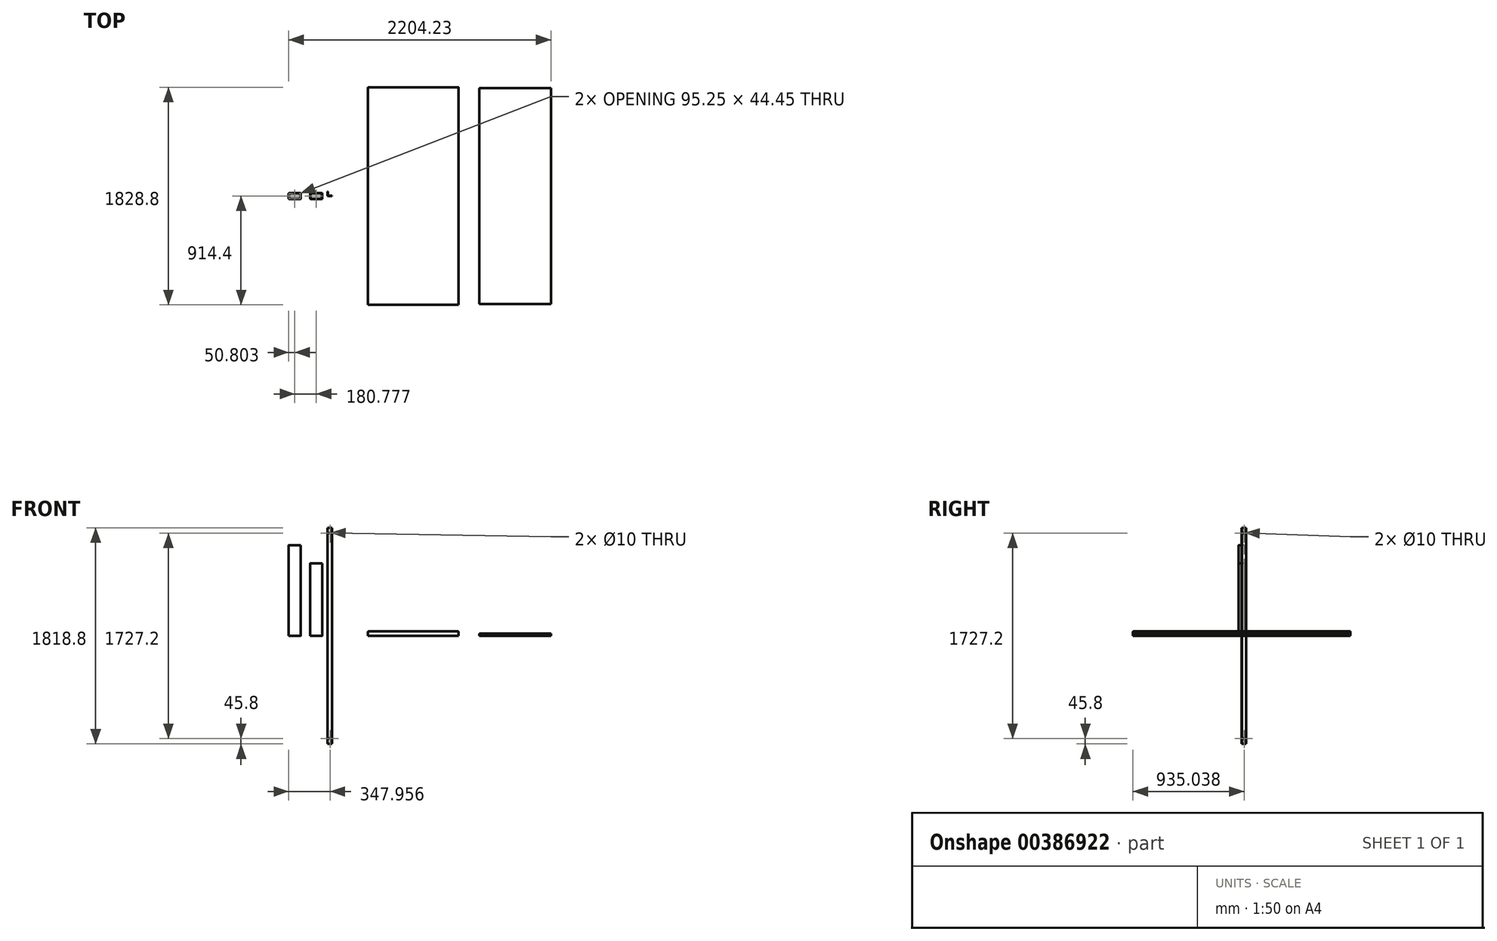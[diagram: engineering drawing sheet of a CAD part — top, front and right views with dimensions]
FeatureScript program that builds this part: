
annotation { "Feature Type Name" : "Feature", "Feature Type Description" : "" }
export const myFeature = defineFeature(function(context is Context, id is Id, definition is map)
    precondition{}
    {
        {
            var Q0;
            Q0=qCreatedBy(makeId("Top.planeOp"),FACE);
            var sketch = newSketch(context, id + "F0", { "sketchPlane" : qUnion([Q0])});
            skPoint(sketch, "E0.middle", {"position": v(-180.78, 0) * mm});
            skLineSegment(sketch, "E1.bottom", {"start": v(-134.98, 25.4) * mm, "end": v(-226.58, 25.4) * mm});
            skLineSegment(sketch, "E1.top", {"start": v(-134.98, -25.4) * mm, "end": v(-226.58, -25.4) * mm});
            skLineSegment(sketch, "E1.left", {"start": v(-129.98, 20.4) * mm, "end": v(-129.98, -20.4) * mm});
            skLineSegment(sketch, "E1.right", {"start": v(-231.58, 20.4) * mm, "end": v(-231.58, -20.4) * mm});
            skLineSegment(sketch, "E2.0", {"start": v(-138.15, 22.22) * mm, "end": v(-223.4, 22.22) * mm});
            skLineSegment(sketch, "E2.1", {"start": v(-133.15, 17.22) * mm, "end": v(-133.15, -17.22) * mm});
            skLineSegment(sketch, "E2.2", {"start": v(-138.15, -22.23) * mm, "end": v(-223.4, -22.23) * mm});
            skLineSegment(sketch, "E2.3", {"start": v(-228.4, 17.22) * mm, "end": v(-228.4, -17.22) * mm});
            skPoint(sketch, "E3.visualSharp", {"position": v(-231.58, 25.4) * mm});
            skArc(sketch, "E3.filletArc", {"start": v(-226.58, 25.4) * mm, "mid": v(-230.11, 23.94) * mm, "end": v(-231.58, 20.4) * mm});
            skPoint(sketch, "E4.visualSharp", {"position": v(-129.98, 25.4) * mm});
            skArc(sketch, "E4.filletArc", {"start": v(-129.98, 20.4) * mm, "mid": v(-131.44, 23.94) * mm, "end": v(-134.98, 25.4) * mm});
            skPoint(sketch, "E5.visualSharp", {"position": v(-129.98, -25.4) * mm});
            skArc(sketch, "E5.filletArc", {"start": v(-134.98, -25.4) * mm, "mid": v(-131.44, -23.94) * mm, "end": v(-129.98, -20.4) * mm});
            skPoint(sketch, "E6.visualSharp", {"position": v(-231.58, -25.4) * mm});
            skArc(sketch, "E6.filletArc", {"start": v(-231.58, -20.4) * mm, "mid": v(-230.11, -23.94) * mm, "end": v(-226.58, -25.4) * mm});
            skPoint(sketch, "E7.visualSharp", {"position": v(-228.4, -22.23) * mm});
            skArc(sketch, "E7.filletArc", {"start": v(-228.4, -17.22) * mm, "mid": v(-226.94, -20.76) * mm, "end": v(-223.4, -22.23) * mm});
            skPoint(sketch, "E8.visualSharp", {"position": v(-228.4, 22.22) * mm});
            skArc(sketch, "E8.filletArc", {"start": v(-223.4, 22.22) * mm, "mid": v(-226.94, 20.76) * mm, "end": v(-228.4, 17.22) * mm});
            skPoint(sketch, "E9.visualSharp", {"position": v(-133.15, 22.22) * mm});
            skArc(sketch, "E9.filletArc", {"start": v(-133.15, 17.22) * mm, "mid": v(-134.62, 20.76) * mm, "end": v(-138.15, 22.22) * mm});
            skPoint(sketch, "E10.visualSharp", {"position": v(-133.15, -22.23) * mm});
            skArc(sketch, "E10.filletArc", {"start": v(-138.15, -22.23) * mm, "mid": v(-134.62, -20.76) * mm, "end": v(-133.15, -17.22) * mm});
            skSolve(sketch);
        }
        {
            var Q0;
            Q0=makeQuery(id+"F0.imprint","IMPRINT",FACE,{"disambiguationData":[TD([[makeQuery(id+"F0.imprint","IMPRINT",EDGE,{"derivedFrom":sQuery(id+"F0.wireOp",EDGE,"E1.bottom")}),1.0]])]});
            extrude(context, id + "F1", {"entities" : qUnion([Q0]), "depth" : 762 * mm});
        }
        {
            var Q0;
            Q0=qCreatedBy(makeId("Top.planeOp"),FACE);
            var sketch = newSketch(context, id + "F2", { "sketchPlane" : qUnion([Q0])});
            skLineSegment(sketch, "E11.bottom", {"start": v(45.8, 25.4) * mm, "end": v(-45.8, 25.4) * mm});
            skLineSegment(sketch, "E11.top", {"start": v(45.8, -25.4) * mm, "end": v(-45.8, -25.4) * mm});
            skLineSegment(sketch, "E11.left", {"start": v(50.8, 20.4) * mm, "end": v(50.8, -20.4) * mm});
            skLineSegment(sketch, "E11.right", {"start": v(-50.8, 20.4) * mm, "end": v(-50.8, -20.4) * mm});
            skPoint(sketch, "E11.middle", {"position": v(0, 0) * mm});
            skLineSegment(sketch, "E12.0", {"start": v(42.62, 22.23) * mm, "end": v(-42.62, 22.23) * mm});
            skLineSegment(sketch, "E12.1", {"start": v(47.62, 17.23) * mm, "end": v(47.62, -17.23) * mm});
            skLineSegment(sketch, "E12.2", {"start": v(42.62, -22.23) * mm, "end": v(-42.62, -22.23) * mm});
            skLineSegment(sketch, "E12.3", {"start": v(-47.62, 17.23) * mm, "end": v(-47.62, -17.23) * mm});
            skPoint(sketch, "E13.visualSharp", {"position": v(-50.8, 25.4) * mm});
            skArc(sketch, "E13.filletArc", {"start": v(-45.8, 25.4) * mm, "mid": v(-49.34, 23.94) * mm, "end": v(-50.8, 20.4) * mm});
            skPoint(sketch, "E14.visualSharp", {"position": v(-47.62, 22.23) * mm});
            skArc(sketch, "E14.filletArc", {"start": v(-42.62, 22.23) * mm, "mid": v(-46.16, 20.76) * mm, "end": v(-47.62, 17.23) * mm});
            skPoint(sketch, "E15.visualSharp", {"position": v(-47.62, -22.23) * mm});
            skArc(sketch, "E15.filletArc", {"start": v(-47.62, -17.23) * mm, "mid": v(-46.16, -20.76) * mm, "end": v(-42.62, -22.22) * mm});
            skPoint(sketch, "E16.visualSharp", {"position": v(-50.8, -25.4) * mm});
            skArc(sketch, "E16.filletArc", {"start": v(-50.8, -20.4) * mm, "mid": v(-49.34, -23.94) * mm, "end": v(-45.8, -25.4) * mm});
            skPoint(sketch, "E17.visualSharp", {"position": v(47.62, -22.23) * mm});
            skArc(sketch, "E17.filletArc", {"start": v(42.62, -22.23) * mm, "mid": v(46.16, -20.76) * mm, "end": v(47.62, -17.23) * mm});
            skPoint(sketch, "E18.visualSharp", {"position": v(47.62, 22.23) * mm});
            skArc(sketch, "E18.filletArc", {"start": v(47.62, 17.23) * mm, "mid": v(46.16, 20.76) * mm, "end": v(42.62, 22.22) * mm});
            skPoint(sketch, "E19.visualSharp", {"position": v(50.8, 25.4) * mm});
            skArc(sketch, "E19.filletArc", {"start": v(50.8, 20.4) * mm, "mid": v(49.34, 23.94) * mm, "end": v(45.8, 25.4) * mm});
            skPoint(sketch, "E20.visualSharp", {"position": v(50.8, -25.4) * mm});
            skArc(sketch, "E20.filletArc", {"start": v(45.8, -25.4) * mm, "mid": v(49.34, -23.94) * mm, "end": v(50.8, -20.4) * mm});
            skSolve(sketch);
        }
        {
            var Q0;
            Q0 = qSketchRegion(id + "F2", true);
            extrude(context, id + "F3", {"entities" : qUnion([Q0]), "depth" : 609.6 * mm});
        }
        {
            var Q0;
            Q0=qCreatedBy(makeId("Top.planeOp"),FACE);
            var sketch = newSketch(context, id + "F4", { "sketchPlane" : qUnion([Q0])});
            skLineSegment(sketch, "E21", {"start": v(95.74, 0) * mm, "end": v(95.74, 38.1) * mm});
            skLineSegment(sketch, "E22", {"start": v(95.74, 38.1) * mm, "end": v(98.91, 38.1) * mm});
            skLineSegment(sketch, "E23", {"start": v(98.91, 38.1) * mm, "end": v(98.91, 3.18) * mm});
            skLineSegment(sketch, "E24", {"start": v(98.91, 3.18) * mm, "end": v(133.84, 3.18) * mm});
            skLineSegment(sketch, "E25", {"start": v(133.84, 3.18) * mm, "end": v(133.84, 0) * mm});
            skLineSegment(sketch, "E26", {"start": v(133.84, 0) * mm, "end": v(95.74, 0) * mm});
            skSolve(sketch);
        }
        {
            var Q0;
            Q0 = qSketchRegion(id + "F4", true);
            extrude(context, id + "F5", {"entities" : qUnion([Q0]), "depth" : 1828.8 * mm - 10 * mm, "symmetric" : true});
        }
        {
            var Q0;
            Q0=qCreatedBy(makeId("Front.planeOp"),FACE);
            var sketch = newSketch(context, id + "F6", { "sketchPlane" : qUnion([Q0])});
            skLineSegment(sketch, "E27.bottom", {"start": v(433.88, 0) * mm, "end": v(1195.88, 0) * mm});
            skLineSegment(sketch, "E27.top", {"start": v(433.88, 38.1) * mm, "end": v(1195.88, 38.1) * mm});
            skLineSegment(sketch, "E27.left", {"start": v(433.88, 0) * mm, "end": v(433.88, 38.1) * mm});
            skLineSegment(sketch, "E27.right", {"start": v(1195.88, 0) * mm, "end": v(1195.88, 38.1) * mm});
            skSolve(sketch);
        }
        {
            var Q0;
            Q0 = qSketchRegion(id + "F6", true);
            extrude(context, id + "F7", {"entities" : qUnion([Q0]), "depth" : 1828.8 * mm, "symmetric" : true});
        }
        {
            var Q0;
            Q0=makeQuery(id+"F7.opExtrude","SWEPT_FACE",FACE,{"disambiguationData":[OSD([sQuery(id+"F6.wireOp",EDGE,"E27.top")])]});
            fillet(context, id + "F8", {"entities" : qUnion([Q0]), "radius" : 6 * mm, "tangentPropagation" : true, "allowEdgeOverflow" : false});
        }
        {
            var Q0;
            Q0=qCreatedBy(makeId("Front.planeOp"),FACE);
            var sketch = newSketch(context, id + "F9", { "sketchPlane" : qUnion([Q0])});
            skLineSegment(sketch, "E28.bottom", {"start": v(1369.4, 0) * mm, "end": v(1972.65, 0) * mm});
            skLineSegment(sketch, "E28.top", {"start": v(1369.4, 19.05) * mm, "end": v(1972.65, 19.05) * mm});
            skLineSegment(sketch, "E28.left", {"start": v(1369.4, 0) * mm, "end": v(1369.4, 19.05) * mm});
            skLineSegment(sketch, "E28.right", {"start": v(1972.65, 0) * mm, "end": v(1972.65, 19.05) * mm});
            skSolve(sketch);
        }
        {
            var Q0;
            Q0=makeQuery(id+"F5.opExtrude","SWEPT_FACE",FACE,{"disambiguationData":[OSD([sQuery(id+"F4.wireOp",EDGE,"E23")])]});
            var sketch = newSketch(context, id + "F10", { "sketchPlane" : qUnion([Q0])});
            skCircle(sketch, "E29", {"center": v(20.64, 863.6) * mm, "radius": 5 * mm});
            skPoint(sketch, "E29.centerSnap0", {"position": v(20.64, 909.4) * mm});
            skCircle(sketch, "E30", {"center": v(20.64, -863.6) * mm, "radius": 5 * mm});
            skPoint(sketch, "E30.centerSnap0", {"position": v(20.64, -909.4) * mm});
            skSolve(sketch);
        }
        {
            var Q0;
            Q0 = qSketchRegion(id + "F10", true);
            extrude(context, id + "F11", {"entities" : qUnion([Q0]), "operationType" : NewBodyOperationType.REMOVE, "endBound" : BoundingType.THROUGH_ALL, "oppositeDirection" : true, "depth" : 25 * mm});
        }
        {
            var Q0;
            Q0=makeQuery(id+"F5.opExtrude","SWEPT_FACE",FACE,{"disambiguationData":[OSD([sQuery(id+"F4.wireOp",EDGE,"E24")])]});
            var sketch = newSketch(context, id + "F12", { "sketchPlane" : qUnion([Q0])});
            skCircle(sketch, "E31", {"center": v(-116.38, 863.6) * mm, "radius": 5 * mm});
            skPoint(sketch, "E31.centerSnap0", {"position": v(-116.38, 909.4) * mm});
            skCircle(sketch, "E32", {"center": v(-116.38, -863.6) * mm, "radius": 5 * mm});
            skPoint(sketch, "E32.centerSnap0", {"position": v(-116.38, -909.4) * mm});
            skSolve(sketch);
        }
        {
            var Q0;
            Q0 = qSketchRegion(id + "F12", true);
            extrude(context, id + "F13", {"entities" : qUnion([Q0]), "operationType" : NewBodyOperationType.REMOVE, "endBound" : BoundingType.THROUGH_ALL, "oppositeDirection" : true, "depth" : 25 * mm});
        }
        {
            var Q0;
            Q0 = qSketchRegion(id + "F9", true);
            extrude(context, id + "F14", {"entities" : qUnion([Q0]), "depth" : 1818.8 * mm, "symmetric" : true});
        }
    });
